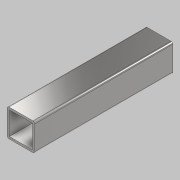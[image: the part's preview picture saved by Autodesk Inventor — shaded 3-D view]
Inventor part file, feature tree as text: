
AUTODESK INVENTOR PART (.ipt)
format: ipt  version: 2021 (Build 250183000, 183)  size: 118,784 bytes
history: native  units: mm
features: extrude x1, fillet x1, plane x1, split x1, sketch x1
ambient origin geometry x8: Origin, YZ Plane, XZ Plane, XY Plane, X Axis, Y Axis, Z Axis, Center Point
bodies: Solid1 (feature_tree)
feature tree (5):
  extrude  "Extrusion1"  Depth=30.0mm
  fillet  "Fillet1"  Radius=15.0mm
  plane  "Work Plane1"
  split  "Split1"
  sketch  "Sketch1"  dims[d0=30.0mm d1=30.0mm d2=15.0mm d3=15.0mm d4=2.5mm d5=1000.0mm d6=0.0mm d7=2.0mm d8=-150.0mm]
